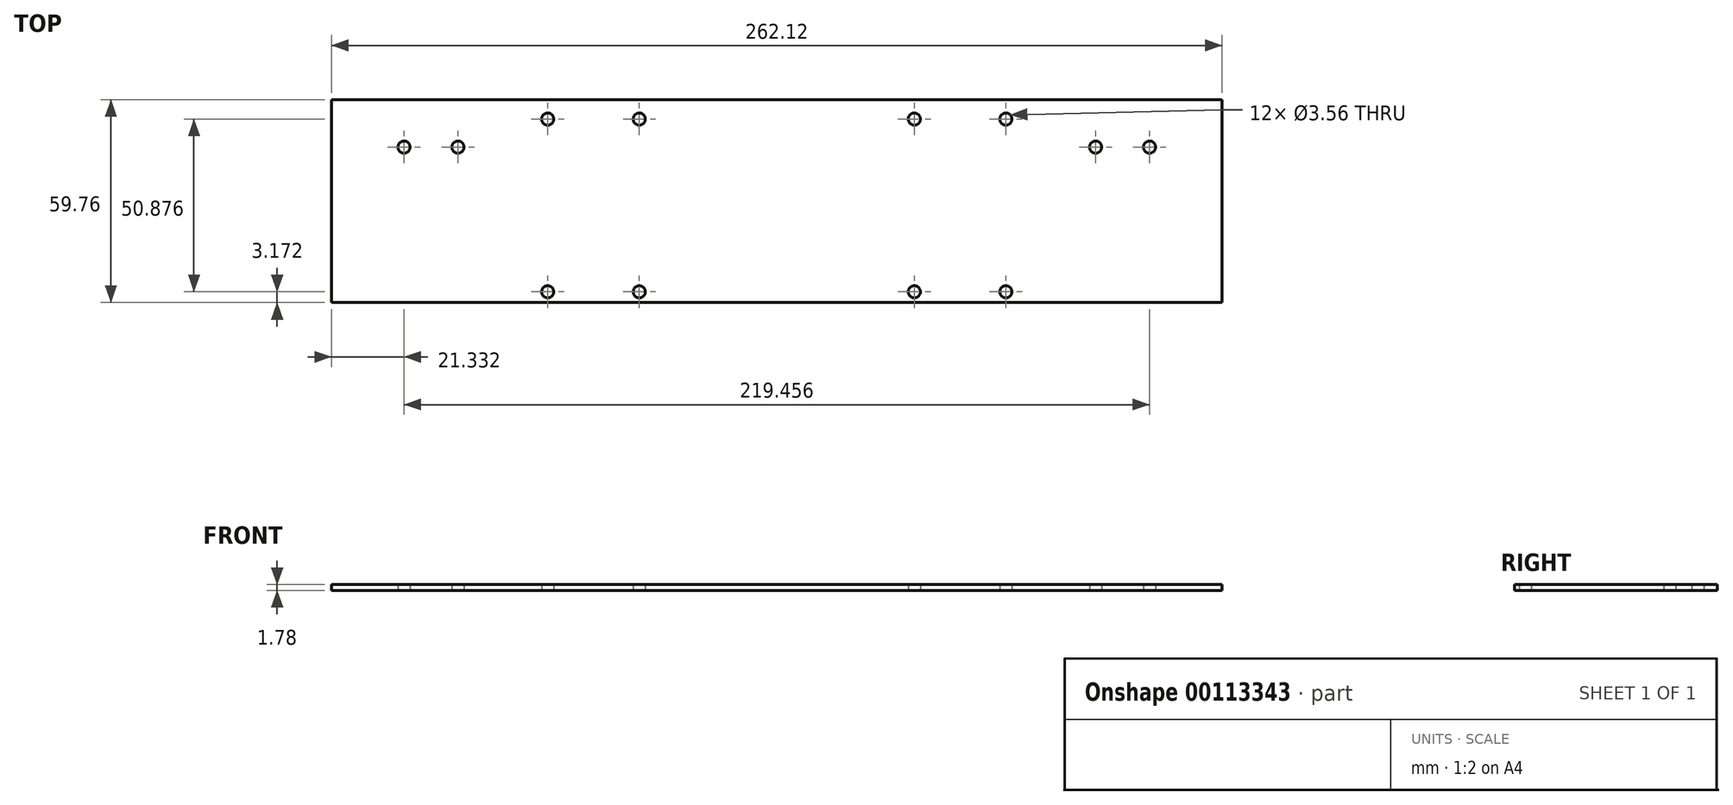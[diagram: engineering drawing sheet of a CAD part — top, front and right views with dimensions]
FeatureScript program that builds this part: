
annotation { "Feature Type Name" : "Feature", "Feature Type Description" : "" }
export const myFeature = defineFeature(function(context is Context, id is Id, definition is map)
    precondition{}
    {
        {
            var Q0;
            Q0=qCreatedBy(makeId("Top.planeOp"),FACE);
            var sketch = newSketch(context, id + "F0", { "sketchPlane" : qUnion([Q0])});
            skLineSegment(sketch, "E0.bottom", {"start": v(131.06, 29.88) * mm, "end": v(-131.06, 29.88) * mm});
            skLineSegment(sketch, "E0.top", {"start": v(131.06, -29.88) * mm, "end": v(-131.06, -29.88) * mm});
            skLineSegment(sketch, "E0.left", {"start": v(131.06, 29.88) * mm, "end": v(131.06, -29.88) * mm});
            skLineSegment(sketch, "E0.right", {"start": v(-131.06, 29.88) * mm, "end": v(-131.06, -29.88) * mm});
            skPoint(sketch, "E0.middle", {"position": v(0, 0) * mm});
            skLineSegment(sketch, "E1", {"start": v(-73.03, -29.88) * mm, "end": v(-73.03, 29.88) * mm, "construction": true});
            skLineSegment(sketch, "E2", {"start": v(-74.8, -29.88) * mm, "end": v(-74.8, 29.88) * mm, "construction": true});
            skLineSegment(sketch, "E3", {"start": v(73.03, -29.88) * mm, "end": v(73.03, 29.88) * mm, "construction": true});
            skLineSegment(sketch, "E4", {"start": v(74.8, -29.88) * mm, "end": v(74.8, 29.88) * mm, "construction": true});
            skCircle(sketch, "E5", {"center": v(-67.44, 24.17) * mm, "radius": 1.78 * mm});
            skCircle(sketch, "E6", {"center": v(-40.49, 24.17) * mm, "radius": 1.78 * mm});
            skCircle(sketch, "E7", {"center": v(-67.44, -26.7) * mm, "radius": 1.78 * mm});
            skCircle(sketch, "E8", {"center": v(-40.49, -26.7) * mm, "radius": 1.78 * mm});
            skCircle(sketch, "E9", {"center": v(40.49, 24.17) * mm, "radius": 1.78 * mm});
            skCircle(sketch, "E10", {"center": v(67.44, 24.17) * mm, "radius": 1.78 * mm});
            skCircle(sketch, "E11", {"center": v(40.49, -26.7) * mm, "radius": 1.78 * mm});
            skCircle(sketch, "E12", {"center": v(67.44, -26.7) * mm, "radius": 1.78 * mm});
            skCircle(sketch, "E13", {"center": v(-109.73, 15.91) * mm, "radius": 1.78 * mm});
            skCircle(sketch, "E14", {"center": v(-93.85, 15.91) * mm, "radius": 1.78 * mm});
            skCircle(sketch, "E15", {"center": v(93.85, 15.91) * mm, "radius": 1.78 * mm});
            skCircle(sketch, "E16", {"center": v(109.73, 15.91) * mm, "radius": 1.78 * mm});
            skLineSegment(sketch, "E17", {"start": v(-128.78, -29.88) * mm, "end": v(-128.78, 29.88) * mm, "construction": true});
            skLineSegment(sketch, "E18", {"start": v(128.78, -29.88) * mm, "end": v(128.78, 29.88) * mm, "construction": true});
            skSolve(sketch);
        }
        {
            var Q0;
            Q0=makeQuery(id+"F0.imprint","IMPRINT",FACE,{"disambiguationData":[TD([[makeQuery(id+"F0.imprint","IMPRINT",EDGE,{"derivedFrom":sQuery(id+"F0.wireOp",EDGE,"E0.bottom")}),1.0]])]});
            extrude(context, id + "F1", {"entities" : qUnion([Q0]), "depth" : 1.78 * mm, "offsetDistance" : 25.4 * mm});
        }
    });
